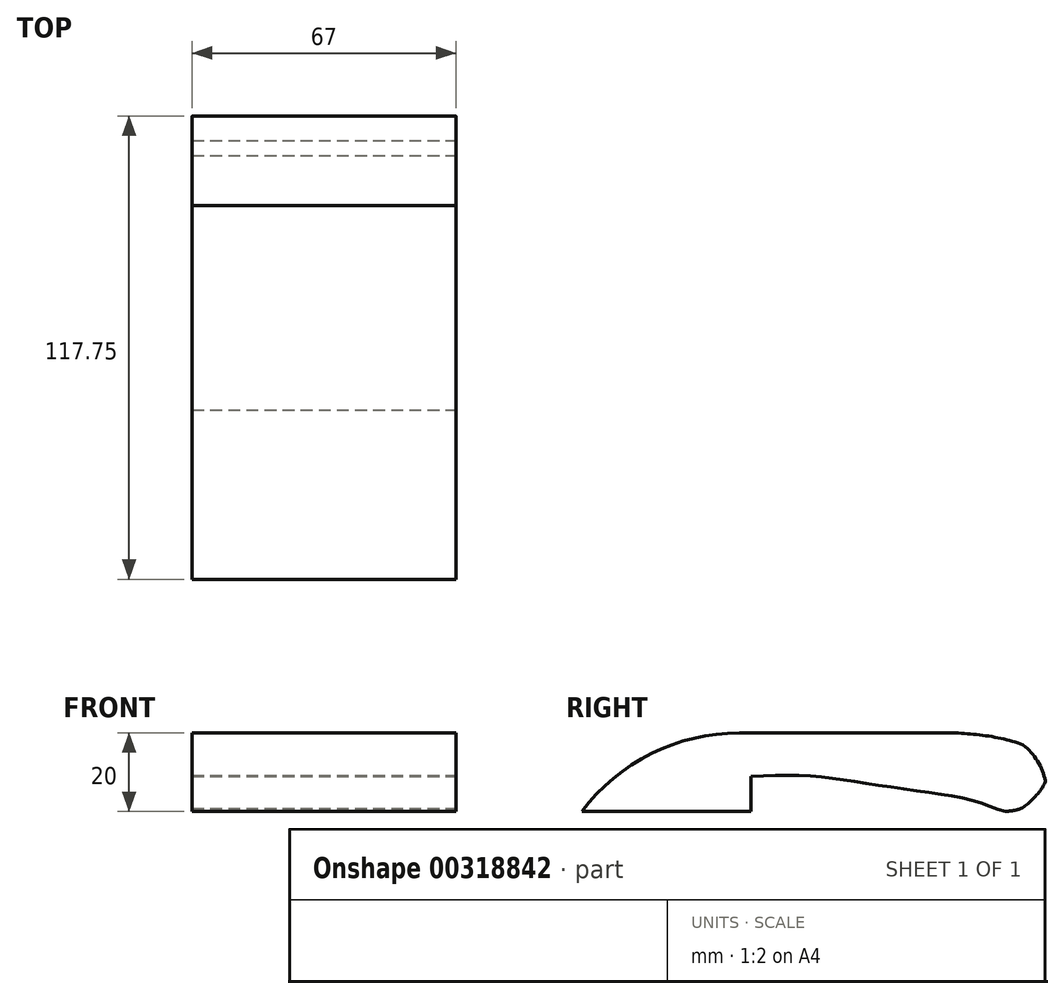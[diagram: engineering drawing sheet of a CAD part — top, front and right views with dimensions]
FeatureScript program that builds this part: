
annotation { "Feature Type Name" : "Feature", "Feature Type Description" : "" }
export const myFeature = defineFeature(function(context is Context, id is Id, definition is map)
    precondition{}
    {
        {
            var Q0;
            Q0=qCreatedBy(makeId("Front.planeOp"),FACE);
            var sketch = newSketch(context, id + "F0", { "sketchPlane" : qUnion([Q0])});
            skLineSegment(sketch, "E0.bottom", {"start": v(-27.16, -37.27) * mm, "end": v(39.84, -37.27) * mm});
            skLineSegment(sketch, "E0.top", {"start": v(-27.16, -57.27) * mm, "end": v(39.84, -57.27) * mm});
            skLineSegment(sketch, "E0.left", {"start": v(-27.16, -37.27) * mm, "end": v(-27.16, -57.27) * mm});
            skLineSegment(sketch, "E0.right", {"start": v(39.84, -37.27) * mm, "end": v(39.84, -57.27) * mm});
            skPoint(sketch, "E0.middle", {"position": v(6.34, -47.27) * mm});
            skSolve(sketch);
        }
        {
            var Q0;
            Q0=makeQuery(id+"F0.imprint","IMPRINT",FACE,{"disambiguationData":[TD([[makeQuery(id+"F0.imprint","IMPRINT",EDGE,{"derivedFrom":sQuery(id+"F0.wireOp",EDGE,"E0.bottom")}),-1.0]])]});
            extrude(context, id + "F1", {"entities" : qUnion([Q0]), "depth" : 118 * mm});
        }
        {
            var Q0;
            Q0=makeQuery(id+"F1.opExtrude","SWEPT_FACE",FACE,{"disambiguationData":[OSD([sQuery(id+"F0.wireOp",EDGE,"E0.right")])]});
            var sketch = newSketch(context, id + "F2", { "sketchPlane" : qUnion([Q0])});
            skLineSegment(sketch, "E1", {"start": v(-118, -57.27) * mm, "end": v(-75, -57.27) * mm});
            skLineSegment(sketch, "E2", {"start": v(-75, -57.27) * mm, "end": v(-75, -48.27) * mm});
            skFitSpline(sketch, "E3", {"points": [v(-75, -48.27) * mm, v(-59.31, -48.27) * mm, v(-45.2, -50.2) * mm, v(-27.45, -52.76) * mm, v(-15.9, -55.32) * mm, v(-8.58, -57.27) * mm, v(-2.5, -53.13) * mm, v(0, -48.27) * mm, v(-3.29, -41.77) * mm, v(-22.97, -37.27) * mm, v(-35.14, -37.27) * mm], "startDerivative": vector(137.84, 4.5) * mm, "endDerivative": vector(-103.99, -4.14) * mm});
            skSolve(sketch);
        }
        {
            var Q0;
            Q0=makeQuery(id+"F1.opExtrude","CAP_EDGE",EDGE,{"disambiguationData":[OSD([sQuery(id+"F0.wireOp",EDGE,"E0.bottom")])],"isStart":false});
            fillet(context, id + "F3", {"entities" : qUnion([Q0]), "radius" : 50 * mm, "tangentPropagation" : true, "allowEdgeOverflow" : false});
        }
        {
            var Q0;
            {var subQ0=sQuery(id+"F0.wireOp",EDGE,"E0.bottom");Q0=makeQuery(id+"F3.opFillet","BLEND_EDGE",EDGE,{"blendedFrom":[makeQuery(id+"F1.opExtrude","CAP_EDGE",EDGE,{"disambiguationData":[OSD([subQ0])],"isStart":false}),makeQuery(id+"F1.opExtrude","SWEPT_FACE",FACE,{"disambiguationData":[OSD([subQ0])]})],"blendedInto":[makeQuery(id+"F1.opExtrude","SWEPT_FACE",FACE,{"disambiguationData":[OSD([subQ0])]})]});}
            var Q1;
            Q1=makeQuery(id+"F1.opExtrude","CAP_EDGE",EDGE,{"disambiguationData":[OSD([sQuery(id+"F0.wireOp",EDGE,"E0.bottom")])],"isStart":true});
            fillet(context, id + "F4", {"entities" : qUnion([Q0, Q1]), "radius" : 15 * mm, "tangentPropagation" : true, "allowEdgeOverflow" : false});
        }
        {
            var Q0;
            Q0=makeQuery(id+"F1.opExtrude","CAP_EDGE",EDGE,{"disambiguationData":[OSD([sQuery(id+"F0.wireOp",EDGE,"E0.top")])],"isStart":true});
            fillet(context, id + "F5", {"entities" : qUnion([Q0]), "radius" : 15 * mm, "tangentPropagation" : true, "allowEdgeOverflow" : false});
        }
        {
            var Q0;
            {var subQ0=sQuery(id+"F2.wireOp",EDGE,"E2");Q0=makeQuery(id+"F2.imprint","IMPRINT",FACE,{"disambiguationData":[TD([[makeQuery(id+"F2.imprint","IMPRINT",EDGE,{"derivedFrom":subQ0}),-1.0]])]});}
            var Q1;
            {var subQ0=sQuery(id+"F2.wireOp",EDGE,"E3");var subQ1=sQuery(id+"F0.wireOp",EDGE,"E0.right");var subQ4=makeQuery(id+"F1.opExtrude","CAP_EDGE",EDGE,{"disambiguationData":[OSD([subQ1])],"isStart":true});var subQ5=makeQuery(id+"F2.imprint","INTERSECT",VERTEX,{"disambiguationData":[OD(0.0)],"derivedFrom":[subQ4,subQ0]});Q1=makeQuery(id+"F2.imprint","IMPRINT",FACE,{"disambiguationData":[TD([[makeQuery(id+"F2.imprint","IMPRINT",EDGE,{"disambiguationData":[TD([[subQ5,1.0]])],"derivedFrom":subQ0}),-1.0]])]});}
            var Q2;
            {var subQ0=sQuery(id+"F2.wireOp",EDGE,"E3");var subQ1=sQuery(id+"F0.wireOp",EDGE,"E0.right");var subQ2=makeQuery(id+"F1.opExtrude","CAP_EDGE",EDGE,{"disambiguationData":[OSD([subQ1])],"isStart":true});var subQ3=makeQuery(id+"F2.imprint","INTERSECT",VERTEX,{"disambiguationData":[OD(1.0)],"derivedFrom":[subQ2,subQ0]});Q2=makeQuery(id+"F2.imprint","IMPRINT",FACE,{"disambiguationData":[TD([[makeQuery(id+"F2.imprint","IMPRINT",EDGE,{"disambiguationData":[TD([[subQ3,-1.0]])],"derivedFrom":subQ0}),-1.0]])]});}
            extrude(context, id + "F6", {"entities" : qUnion([Q0, Q1, Q2]), "operationType" : NewBodyOperationType.REMOVE, "endBound" : BoundingType.THROUGH_ALL, "oppositeDirection" : true, "depth" : 25 * mm});
        }
        {
            var Q0;
            Q0=makeQuery(id+"F4.opFillet","BLEND_FACE",FACE,{"disambiguationData":[OSD([sQuery(id+"F0.wireOp",EDGE,"E0.bottom")])]});
            fillet(context, id + "F7", {"entities" : qUnion([Q0]), "radius" : 0.02 * mm, "tangentPropagation" : true, "allowEdgeOverflow" : false});
        }
    });
